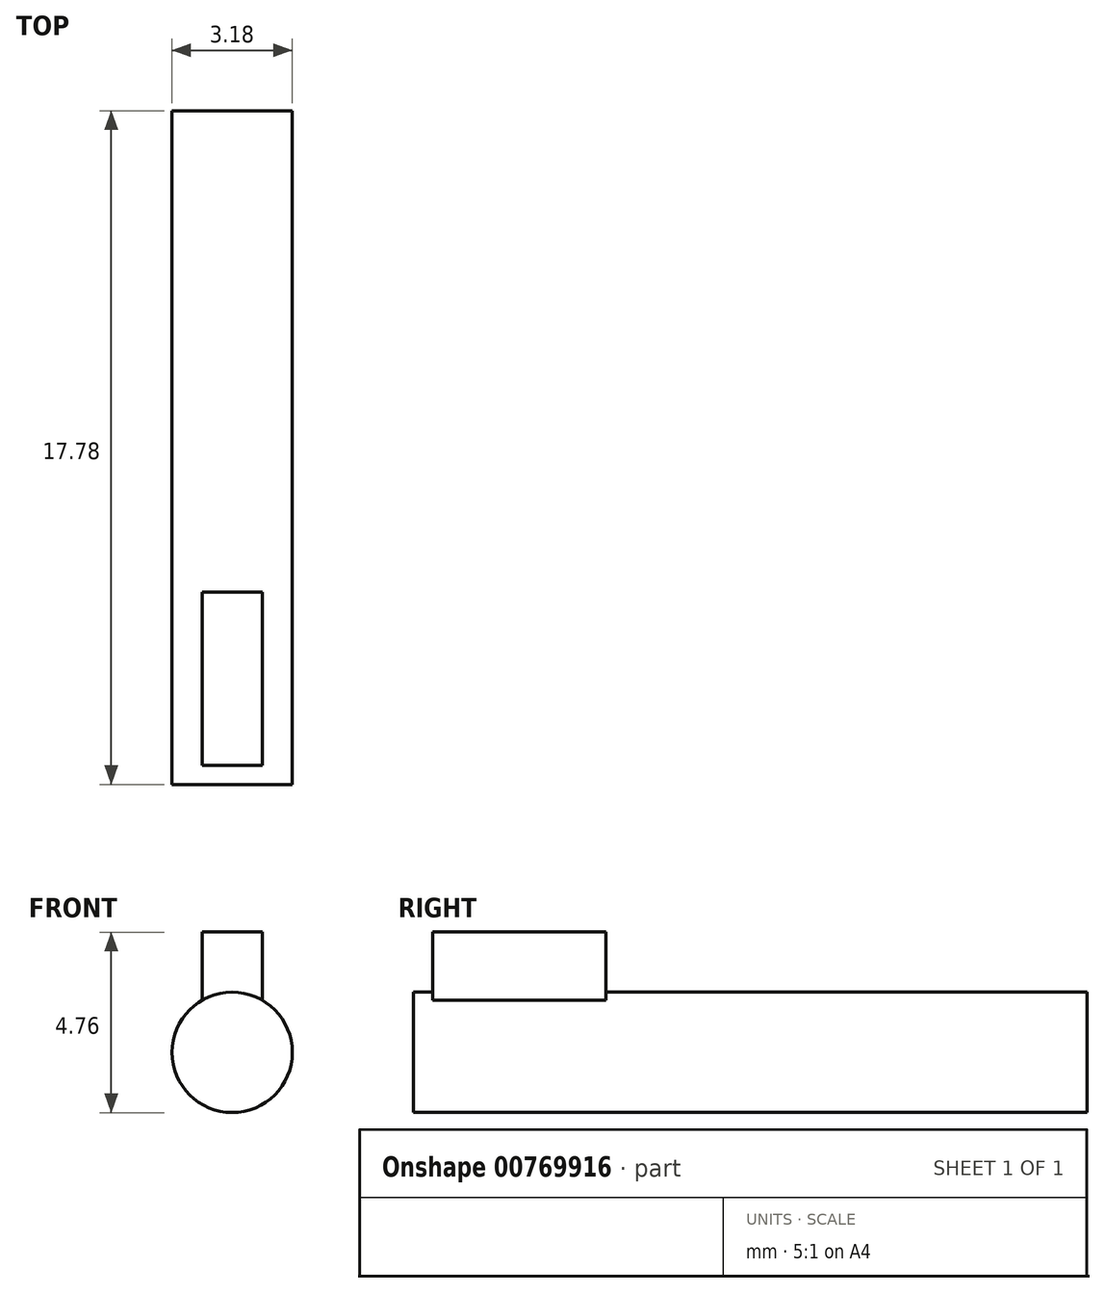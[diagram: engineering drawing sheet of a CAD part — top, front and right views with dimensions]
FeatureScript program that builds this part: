
annotation { "Feature Type Name" : "Feature", "Feature Type Description" : "" }
export const myFeature = defineFeature(function(context is Context, id is Id, definition is map)
    precondition{}
    {
        {
            var Q0;
            Q0=qCreatedBy(makeId("Front.planeOp"),FACE);
            var sketch = newSketch(context, id + "F0", { "sketchPlane" : qUnion([Q0])});
            skCircle(sketch, "E0", {"center": v(0, 0) * mm, "radius": 1.59 * mm});
            skLineSegment(sketch, "E1", {"start": v(-0.8, 1.37) * mm, "end": v(-0.8, 3.17) * mm});
            skLineSegment(sketch, "E2", {"start": v(-0.8, 3.17) * mm, "end": v(0.8, 3.17) * mm});
            skLineSegment(sketch, "E3", {"start": v(0.8, 3.17) * mm, "end": v(0.8, 1.37) * mm});
            skSolve(sketch);
        }
        {
            var Q0;
            {var subQ0=sQuery(id+"F0.wireOp",EDGE,"E1");Q0=makeQuery(id+"F0.imprint","IMPRINT",FACE,{"disambiguationData":[TD([[makeQuery(id+"F0.imprint","IMPRINT",EDGE,{"derivedFrom":subQ0}),-1.0]])]});}
            extrude(context, id + "F1", {"entities" : qUnion([Q0]), "depth" : 4.57 * mm, "offsetDistance" : 25.4 * mm});
        }
        {
            var Q0;
            {var subQ0=sQuery(id+"F0.wireOp",EDGE,"E0");var subQ1=makeQuery(id+"F0.imprint","INTERSECT",VERTEX,{"derivedFrom":[subQ0,sQuery(id+"F0.wireOp",EDGE,"E1")]});Q0=makeQuery(id+"F0.imprint","IMPRINT",FACE,{"disambiguationData":[TD([[makeQuery(id+"F0.imprint","IMPRINT",EDGE,{"disambiguationData":[TD([[subQ1,1.0]])],"derivedFrom":subQ0}),1.0]])]});}
            extrude(context, id + "F2", {"entities" : qUnion([Q0]), "operationType" : NewBodyOperationType.ADD, "depth" : 5.08 * mm, "offsetDistance" : 25.4 * mm});
        }
        {
            var Q0;
            {var subQ0=sQuery(id+"F0.wireOp",EDGE,"E0");Q0=makeQuery(id+"F2.boolean.opBoolean","MERGE",FACE,{"derivedFrom":[makeQuery(id+"F1.opExtrude","CAP_FACE",FACE,{"disambiguationData":[OSD([subQ0,sQuery(id+"F0.wireOp",EDGE,"E1"),sQuery(id+"F0.wireOp",EDGE,"E2"),sQuery(id+"F0.wireOp",EDGE,"E3")])],"isStart":true}),makeQuery(id+"F2.opExtrude","CAP_FACE",FACE,{"disambiguationData":[OSD([subQ0])],"isStart":true})]});}
            var sketch = newSketch(context, id + "F3", { "sketchPlane" : qUnion([Q0])});
            skCircle(sketch, "E4", {"center": v(0, 0) * mm, "radius": 1.59 * mm});
            skSolve(sketch);
        }
        {
            var Q0;
            Q0=qSketchRegion(id+"F3",true);
            extrude(context, id + "F4", {"entities" : qUnion([Q0]), "operationType" : NewBodyOperationType.ADD, "depth" : 12.7 * mm, "offsetDistance" : 25.4 * mm});
        }
    });
